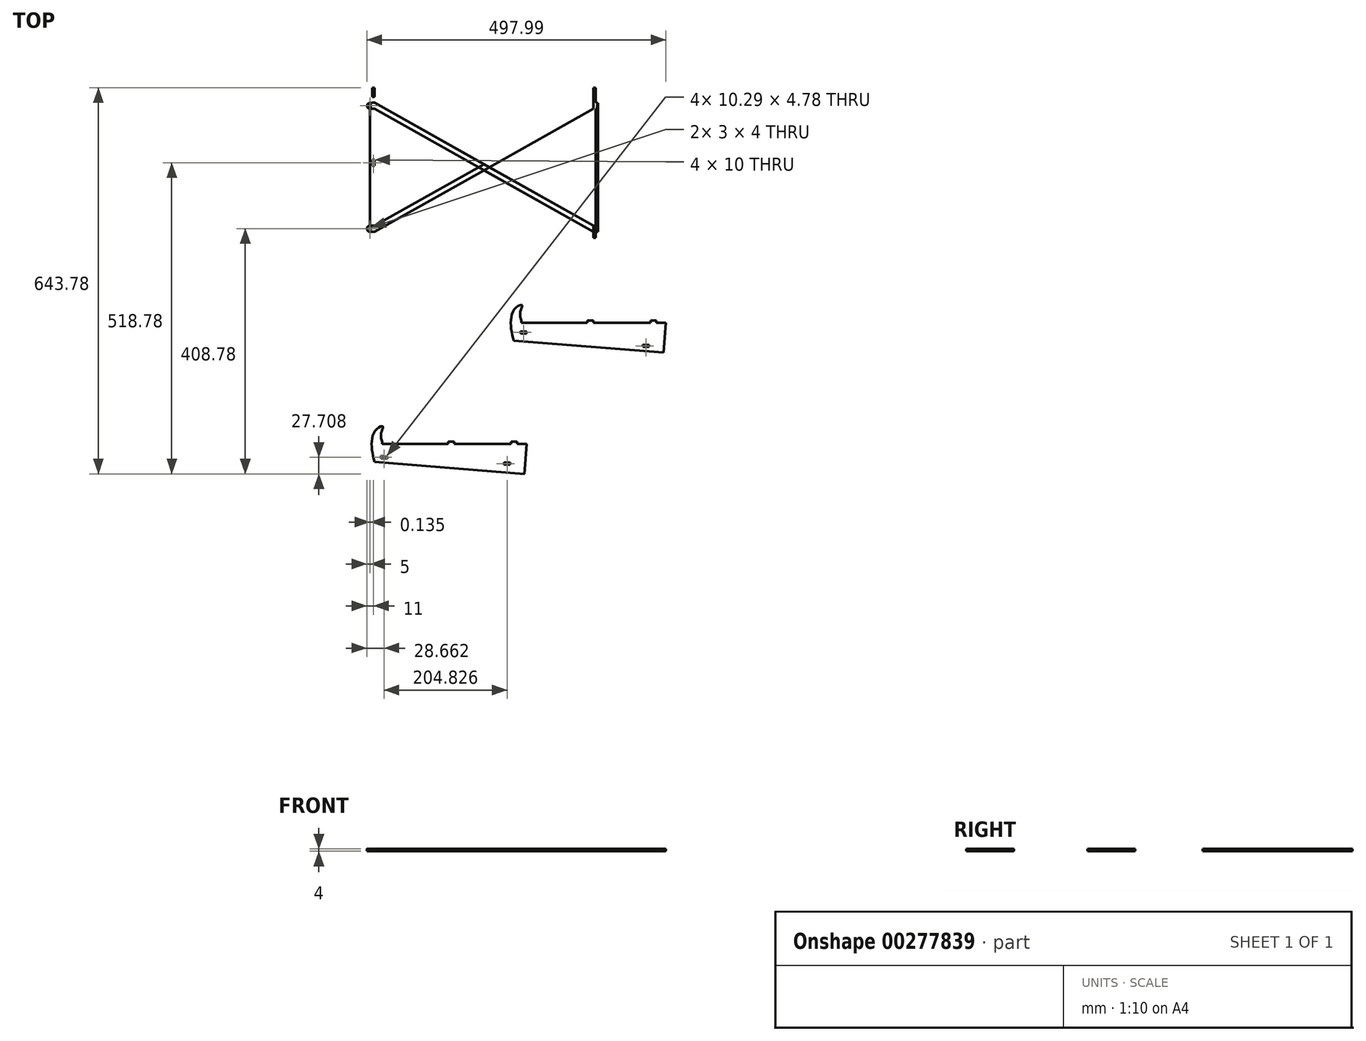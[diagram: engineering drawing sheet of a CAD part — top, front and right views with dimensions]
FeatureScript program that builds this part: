
annotation { "Feature Type Name" : "Feature", "Feature Type Description" : "" }
export const myFeature = defineFeature(function(context is Context, id is Id, definition is map)
    precondition{}
    {
        {
            var Q0;
            Q0=qCreatedBy(makeId("Top.planeOp"),FACE);
            var sketch = newSketch(context, id + "F0", { "sketchPlane" : qUnion([Q0])});
            skLineSegment(sketch, "E0.bottom", {"start": v(190, 125) * mm, "end": v(-190, 125) * mm});
            skLineSegment(sketch, "E0.top", {"start": v(190, -125) * mm, "end": v(-190, -125) * mm});
            skLineSegment(sketch, "E0.left", {"start": v(190, 125) * mm, "end": v(190, -125) * mm});
            skLineSegment(sketch, "E0.right", {"start": v(-190, 125) * mm, "end": v(-190, -125) * mm});
            skPoint(sketch, "E0.middle", {"position": v(0, 0) * mm});
            skLineSegment(sketch, "E1.right", {"start": v(-190, 125) * mm, "end": v(-190, -108) * mm});
            skLineSegment(sketch, "E2.bottom", {"start": v(-190, -125) * mm, "end": v(-186, -125) * mm});
            skLineSegment(sketch, "E2.top", {"start": v(-190, 125) * mm, "end": v(-186, 125) * mm});
            skLineSegment(sketch, "E2.left", {"start": v(-190, -125) * mm, "end": v(-190, -112) * mm});
            skLineSegment(sketch, "E2.right", {"start": v(-186, -125) * mm, "end": v(-186, -115) * mm});
            skLineSegment(sketch, "E3.bottom", {"start": v(190, -125) * mm, "end": v(186, -125) * mm});
            skLineSegment(sketch, "E3.top", {"start": v(190, 125) * mm, "end": v(186, 125) * mm});
            skLineSegment(sketch, "E3.left", {"start": v(190, -125) * mm, "end": v(190, 125) * mm});
            skLineSegment(sketch, "E3.right", {"start": v(186, -125) * mm, "end": v(186, 125) * mm});
            skLineSegment(sketch, "E4", {"start": v(49.8, -296.66) * mm, "end": v(299, -316.6) * mm});
            skLineSegment(sketch, "E5", {"start": v(299, -316.6) * mm, "end": v(303, -266.76) * mm});
            skLineSegment(sketch, "E6", {"start": v(303, -266.76) * mm, "end": v(287.2, -266.76) * mm});
            skLineSegment(sketch, "E7", {"start": v(52.2, -266.76) * mm, "end": v(49.8, -296.66) * mm, "construction": true});
            skLineSegment(sketch, "E8", {"start": v(0, 0) * mm, "end": v(0, 125) * mm, "construction": true});
            skLineSegment(sketch, "E9", {"start": v(0, 0) * mm, "end": v(0, -125) * mm, "construction": true});
            skLineSegment(sketch, "E10.bottom", {"start": v(-186, 125) * mm, "end": v(-182, 125) * mm});
            skLineSegment(sketch, "E10.top", {"start": v(-186, -125) * mm, "end": v(-182, -125) * mm});
            skLineSegment(sketch, "E10.left", {"start": v(-186, 125) * mm, "end": v(-186, 100) * mm});
            skLineSegment(sketch, "E10.right", {"start": v(-182, 125) * mm, "end": v(-182, 100) * mm});
            skLineSegment(sketch, "E11.MirrorCS", {"start": v(182, 125) * mm, "end": v(182, -125) * mm});
            skLineSegment(sketch, "E12", {"start": v(-186, -115) * mm, "end": v(-182, -115) * mm});
            skLineSegment(sketch, "E13", {"start": v(-186, 0) * mm, "end": v(186, 0) * mm, "construction": true});
            skLineSegment(sketch, "E14", {"start": v(-183.8, 0) * mm, "end": v(-183.8, 5) * mm, "construction": true});
            skLineSegment(sketch, "E15", {"start": v(-186, 5) * mm, "end": v(-182, 5) * mm});
            skLineSegment(sketch, "E16.MirrorCS", {"start": v(-186, -5) * mm, "end": v(-182, -5) * mm});
            skLineSegment(sketch, "E17", {"start": v(-186, 110) * mm, "end": v(-182, 110) * mm});
            skLineSegment(sketch, "E18", {"start": v(-186, 100) * mm, "end": v(-182, 100) * mm});
            skLineSegment(sketch, "E19", {"start": v(52.2, -266.76) * mm, "end": v(52.2, -242.76) * mm, "construction": true});
            skLineSegment(sketch, "E20", {"start": v(52.2, -242.76) * mm, "end": v(62.16, -243.56) * mm, "construction": true});
            skLineSegment(sketch, "E21", {"start": v(62.16, -243.56) * mm, "end": v(62.16, -266.76) * mm, "construction": true});
            skLineSegment(sketch, "E22.bottom", {"start": v(62.16, -266.76) * mm, "end": v(172.2, -266.76) * mm, "construction": true});
            skLineSegment(sketch, "E22.top", {"start": v(52.2, -262.76) * mm, "end": v(303, -262.76) * mm, "construction": true});
            skLineSegment(sketch, "E22.left", {"start": v(52.2, -266.76) * mm, "end": v(52.2, -262.76) * mm, "construction": true});
            skLineSegment(sketch, "E22.right", {"start": v(303, -266.76) * mm, "end": v(303, -262.76) * mm, "construction": true});
            skFitSpline(sketch, "E23", {"points": [v(49.8, -296.66) * mm, v(44.72, -265.8) * mm, v(52.2, -242.76) * mm, v(62.86, -237.24) * mm, v(62.38, -242.76) * mm, v(62.16, -262.76) * mm], "startDerivative": vector(-32.9, 108.57) * mm, "endDerivative": vector(52.9, -154.73) * mm});
            skLineSegment(sketch, "E24", {"start": v(62.16, -262.76) * mm, "end": v(62.16, -266.76) * mm});
            skLineSegment(sketch, "E25", {"start": v(302.2, -266.76) * mm, "end": v(302.2, -262.76) * mm, "construction": true});
            skLineSegment(sketch, "E26", {"start": v(287.2, -266.76) * mm, "end": v(287.2, -262.76) * mm});
            skLineSegment(sketch, "E27", {"start": v(287.2, -262.76) * mm, "end": v(277.2, -262.76) * mm});
            skLineSegment(sketch, "E28", {"start": v(277.2, -262.76) * mm, "end": v(277.2, -266.76) * mm});
            skLineSegment(sketch, "E29", {"start": v(182.2, -266.76) * mm, "end": v(182.2, -262.76) * mm});
            skLineSegment(sketch, "E30", {"start": v(172.2, -266.76) * mm, "end": v(172.2, -262.76) * mm});
            skLineSegment(sketch, "E31", {"start": v(172.2, -262.76) * mm, "end": v(182.2, -262.76) * mm});
            skLineSegment(sketch, "E32", {"start": v(-182, -105) * mm, "end": v(-186, -105) * mm});
            skLineSegment(sketch, "E33", {"start": v(-186, 90) * mm, "end": v(-182, 90) * mm});
            skLineSegment(sketch, "E34.MirrorCS", {"start": v(186, 125) * mm, "end": v(182, 125) * mm});
            skLineSegment(sketch, "E35.MirrorCS", {"start": v(186, -125) * mm, "end": v(182, -125) * mm});
            skLineSegment(sketch, "E36.MirrorCS", {"start": v(-190, -125) * mm, "end": v(190, -125) * mm});
            skLineSegment(sketch, "E37.MirrorCS", {"start": v(186, 110) * mm, "end": v(182, 110) * mm});
            skLineSegment(sketch, "E38.MirrorCS", {"start": v(183.8, 0) * mm, "end": v(183.8, 5) * mm, "construction": true});
            skLineSegment(sketch, "E39.MirrorCS", {"start": v(186, 100) * mm, "end": v(182, 100) * mm});
            skLineSegment(sketch, "E40.MirrorCS", {"start": v(182, -105) * mm, "end": v(186, -105) * mm});
            skLineSegment(sketch, "E41.MirrorCS", {"start": v(186, -5) * mm, "end": v(182, -5) * mm});
            skLineSegment(sketch, "E42.MirrorCS", {"start": v(186, 90) * mm, "end": v(182, 90) * mm});
            skLineSegment(sketch, "E43.MirrorCS", {"start": v(186, 5) * mm, "end": v(182, 5) * mm});
            skLineSegment(sketch, "E44.MirrorCS", {"start": v(186, -115) * mm, "end": v(182, -115) * mm});
            skLineSegment(sketch, "E45", {"start": v(-182, -115) * mm, "end": v(182, 90) * mm});
            skLineSegment(sketch, "E46", {"start": v(-182, -105) * mm, "end": v(182, 100) * mm});
            skLineSegment(sketch, "E47", {"start": v(-182, 90) * mm, "end": v(182, -115) * mm});
            skLineSegment(sketch, "E48", {"start": v(182, -105) * mm, "end": v(-182, 100) * mm});
            skLineSegment(sketch, "E49.trimOffspring", {"start": v(-186, -115) * mm, "end": v(-186, -125) * mm});
            skLineSegment(sketch, "E50.trimOffspring", {"start": v(-186, -105) * mm, "end": v(-186, 90) * mm});
            skLineSegment(sketch, "E51", {"start": v(-186, -105) * mm, "end": v(-190, -105) * mm});
            skLineSegment(sketch, "E52", {"start": v(-186, -115) * mm, "end": v(-190, -115) * mm});
            skArc(sketch, "E53", {"start": v(-190, -105) * mm, "mid": v(-195, -110) * mm, "end": v(-190, -115) * mm});
            skArc(sketch, "E54", {"start": v(-190, 99.76) * mm, "mid": v(-194.75, 94.88) * mm, "end": v(-190, 90) * mm});
            skLineSegment(sketch, "E55.trimOffspring", {"start": v(-186, 100) * mm, "end": v(-186, 125) * mm});
            skLineSegment(sketch, "E56.trimOffspring", {"start": v(-186, 90) * mm, "end": v(-186, -105) * mm});
            skLineSegment(sketch, "E57.trimOffspring", {"start": v(-182, 90) * mm, "end": v(-182, -125) * mm});
            skLineSegment(sketch, "E58.MirrorCS", {"start": v(186, -125) * mm, "end": v(186, -115) * mm});
            skLineSegment(sketch, "E59.MirrorCS", {"start": v(186, -115) * mm, "end": v(186, -125) * mm});
            skLineSegment(sketch, "E60.MirrorCS", {"start": v(186, -115) * mm, "end": v(190, -115) * mm});
            skLineSegment(sketch, "E61.MirrorCS", {"start": v(186, -105) * mm, "end": v(190, -105) * mm});
            skArc(sketch, "E62.MirrorCS", {"start": v(190, -105) * mm, "mid": v(195, -110) * mm, "end": v(190, -115) * mm});
            skLineSegment(sketch, "E63.MirrorCS", {"start": v(186, 100) * mm, "end": v(186, 125) * mm});
            skLineSegment(sketch, "E64.MirrorCS", {"start": v(182, 125) * mm, "end": v(182, 100) * mm});
            skLineSegment(sketch, "E65.MirrorCS", {"start": v(186, 125) * mm, "end": v(186, 100) * mm});
            skArc(sketch, "E66.MirrorCS", {"start": v(190, 99.76) * mm, "mid": v(194.75, 94.88) * mm, "end": v(190, 90) * mm});
            skLineSegment(sketch, "E67.MirrorCS", {"start": v(186, 90) * mm, "end": v(186, -105) * mm});
            skLineSegment(sketch, "E68.MirrorCS", {"start": v(186, -105) * mm, "end": v(186, 90) * mm});
            skLineSegment(sketch, "E69.MirrorCS", {"start": v(182, 90) * mm, "end": v(182, -125) * mm});
            skLineSegment(sketch, "E70", {"start": v(186, 100) * mm, "end": v(190, 99.76) * mm});
            skLineSegment(sketch, "E71", {"start": v(186, 90) * mm, "end": v(190, 90) * mm});
            skLineSegment(sketch, "E72", {"start": v(-186, 90) * mm, "end": v(-190, 90) * mm});
            skLineSegment(sketch, "E73", {"start": v(-186, 100) * mm, "end": v(-190, 99.76) * mm});
            skLineSegment(sketch, "E74.trimOffspring", {"start": v(182.2, -266.76) * mm, "end": v(277.2, -266.76) * mm, "construction": true});
            skLineSegment(sketch, "E75.trimOffspring", {"start": v(172.2, -266.76) * mm, "end": v(62.16, -266.76) * mm});
            skLineSegment(sketch, "E76.trimOffspring", {"start": v(287.2, -266.76) * mm, "end": v(303, -266.76) * mm, "construction": true});
            skLineSegment(sketch, "E77.trimOffspring", {"start": v(277.2, -266.76) * mm, "end": v(182.2, -266.76) * mm});
            skLineSegment(sketch, "E78", {"start": v(50.84, -283.7) * mm, "end": v(300.04, -303.64) * mm, "construction": true});
            skLineSegment(sketch, "E79", {"start": v(51.16, -279.72) * mm, "end": v(300.36, -299.66) * mm, "construction": true});
            skLineSegment(sketch, "E80", {"start": v(275.12, -301.65) * mm, "end": v(275.44, -297.66) * mm});
            skLineSegment(sketch, "E81", {"start": v(275.44, -297.66) * mm, "end": v(265.47, -296.86) * mm});
            skLineSegment(sketch, "E82", {"start": v(265.47, -296.86) * mm, "end": v(265.15, -300.85) * mm});
            skLineSegment(sketch, "E83", {"start": v(265.15, -300.85) * mm, "end": v(275.12, -301.65) * mm});
            skLineSegment(sketch, "E84", {"start": v(60.8, -284.5) * mm, "end": v(61.13, -280.52) * mm});
            skLineSegment(sketch, "E85", {"start": v(71.1, -281.31) * mm, "end": v(70.77, -285.3) * mm});
            skLineSegment(sketch, "E86", {"start": v(61.13, -280.52) * mm, "end": v(71.1, -281.31) * mm});
            skLineSegment(sketch, "E87", {"start": v(70.77, -285.3) * mm, "end": v(60.8, -284.5) * mm});
            skLineSegment(sketch, "E88", {"start": v(265.47, -296.86) * mm, "end": v(264.12, -313.81) * mm, "construction": true});
            skLineSegment(sketch, "E89", {"start": v(275.44, -297.66) * mm, "end": v(274.09, -314.6) * mm, "construction": true});
            skLineSegment(sketch, "E90", {"start": v(264.68, -306.83) * mm, "end": v(274.64, -307.63) * mm});
            skLineSegment(sketch, "E91", {"start": v(265, -302.85) * mm, "end": v(274.96, -303.64) * mm});
            skLineSegment(sketch, "E92", {"start": v(265, -302.85) * mm, "end": v(264.68, -306.83) * mm});
            skLineSegment(sketch, "E93", {"start": v(274.96, -303.64) * mm, "end": v(274.64, -307.63) * mm});
            skLineSegment(sketch, "E94", {"start": v(61.13, -280.52) * mm, "end": v(59.77, -297.46) * mm, "construction": true});
            skLineSegment(sketch, "E95", {"start": v(60.65, -286.5) * mm, "end": v(70.62, -287.3) * mm});
            skLineSegment(sketch, "E96", {"start": v(60.33, -290.48) * mm, "end": v(70.3, -291.28) * mm});
            skLineSegment(sketch, "E97", {"start": v(70.3, -291.28) * mm, "end": v(70.62, -287.3) * mm});
            skLineSegment(sketch, "E98", {"start": v(60.65, -286.5) * mm, "end": v(60.33, -290.48) * mm});
            skLineSegment(sketch, "E99", {"start": v(-182, -498.85) * mm, "end": v(67.2, -518.78) * mm});
            skLineSegment(sketch, "E100", {"start": v(67.2, -518.78) * mm, "end": v(71.18, -468.94) * mm});
            skLineSegment(sketch, "E101", {"start": v(71.18, -468.94) * mm, "end": v(55.38, -468.94) * mm});
            skLineSegment(sketch, "E102", {"start": v(-179.62, -468.94) * mm, "end": v(-182, -498.85) * mm, "construction": true});
            skLineSegment(sketch, "E103", {"start": v(-179.62, -468.94) * mm, "end": v(-179.62, -444.94) * mm, "construction": true});
            skLineSegment(sketch, "E104", {"start": v(-179.62, -444.94) * mm, "end": v(-169.65, -445.74) * mm, "construction": true});
            skLineSegment(sketch, "E105", {"start": v(-169.65, -445.74) * mm, "end": v(-169.65, -468.94) * mm, "construction": true});
            skLineSegment(sketch, "E106.bottom", {"start": v(-169.65, -468.94) * mm, "end": v(-59.62, -468.94) * mm, "construction": true});
            skLineSegment(sketch, "E106.top", {"start": v(-179.62, -464.94) * mm, "end": v(71.18, -464.94) * mm, "construction": true});
            skLineSegment(sketch, "E106.left", {"start": v(-179.62, -468.94) * mm, "end": v(-179.62, -464.94) * mm, "construction": true});
            skLineSegment(sketch, "E106.right", {"start": v(71.18, -468.94) * mm, "end": v(71.18, -464.94) * mm, "construction": true});
            skFitSpline(sketch, "E107", {"points": [v(-182, -498.85) * mm, v(-187.09, -467.99) * mm, v(-179.62, -444.94) * mm, v(-168.95, -439.42) * mm, v(-169.43, -444.94) * mm, v(-169.65, -464.94) * mm], "startDerivative": vector(-32.9, 108.57) * mm, "endDerivative": vector(52.9, -154.73) * mm});
            skLineSegment(sketch, "E108", {"start": v(-169.65, -464.94) * mm, "end": v(-169.65, -468.94) * mm});
            skLineSegment(sketch, "E109", {"start": v(70.38, -468.94) * mm, "end": v(70.38, -464.94) * mm, "construction": true});
            skLineSegment(sketch, "E110", {"start": v(55.38, -468.94) * mm, "end": v(55.38, -464.94) * mm});
            skLineSegment(sketch, "E111", {"start": v(55.38, -464.94) * mm, "end": v(45.38, -464.94) * mm});
            skLineSegment(sketch, "E112", {"start": v(45.38, -464.94) * mm, "end": v(45.38, -468.94) * mm});
            skLineSegment(sketch, "E113", {"start": v(-49.62, -468.94) * mm, "end": v(-49.62, -464.94) * mm});
            skLineSegment(sketch, "E114", {"start": v(-59.62, -468.94) * mm, "end": v(-59.62, -464.94) * mm});
            skLineSegment(sketch, "E115", {"start": v(-59.62, -464.94) * mm, "end": v(-49.62, -464.94) * mm});
            skLineSegment(sketch, "E116.trimOffspring", {"start": v(-49.62, -468.94) * mm, "end": v(45.38, -468.94) * mm, "construction": true});
            skLineSegment(sketch, "E117.trimOffspring", {"start": v(-59.62, -468.94) * mm, "end": v(-169.65, -468.94) * mm});
            skLineSegment(sketch, "E118.trimOffspring", {"start": v(55.38, -468.94) * mm, "end": v(71.18, -468.94) * mm, "construction": true});
            skLineSegment(sketch, "E119.trimOffspring", {"start": v(45.38, -468.94) * mm, "end": v(-49.62, -468.94) * mm});
            skLineSegment(sketch, "E120", {"start": v(-180.97, -485.89) * mm, "end": v(68.23, -505.82) * mm, "construction": true});
            skLineSegment(sketch, "E121", {"start": v(-180.65, -481.9) * mm, "end": v(68.55, -501.84) * mm, "construction": true});
            skLineSegment(sketch, "E122", {"start": v(43.31, -503.83) * mm, "end": v(43.63, -499.84) * mm});
            skLineSegment(sketch, "E123", {"start": v(43.63, -499.84) * mm, "end": v(33.66, -499.05) * mm});
            skLineSegment(sketch, "E124", {"start": v(33.66, -499.05) * mm, "end": v(33.34, -503.03) * mm});
            skLineSegment(sketch, "E125", {"start": v(33.34, -503.03) * mm, "end": v(43.31, -503.83) * mm});
            skLineSegment(sketch, "E126", {"start": v(-171, -486.69) * mm, "end": v(-170.68, -482.7) * mm});
            skLineSegment(sketch, "E127", {"start": v(-160.72, -483.5) * mm, "end": v(-161.03, -487.48) * mm});
            skLineSegment(sketch, "E128", {"start": v(-170.68, -482.7) * mm, "end": v(-160.72, -483.5) * mm});
            skLineSegment(sketch, "E129", {"start": v(-161.03, -487.48) * mm, "end": v(-171, -486.69) * mm});
            skLineSegment(sketch, "E130", {"start": v(33.66, -499.05) * mm, "end": v(32.3, -516) * mm, "construction": true});
            skLineSegment(sketch, "E131", {"start": v(43.63, -499.84) * mm, "end": v(42.28, -516.79) * mm, "construction": true});
            skLineSegment(sketch, "E132", {"start": v(32.87, -509.01) * mm, "end": v(42.83, -509.81) * mm});
            skLineSegment(sketch, "E133", {"start": v(33.19, -505.03) * mm, "end": v(43.15, -505.82) * mm});
            skLineSegment(sketch, "E134", {"start": v(33.19, -505.03) * mm, "end": v(32.87, -509.01) * mm});
            skLineSegment(sketch, "E135", {"start": v(43.15, -505.82) * mm, "end": v(42.83, -509.81) * mm});
            skLineSegment(sketch, "E136", {"start": v(-170.68, -482.7) * mm, "end": v(-172.04, -499.64) * mm, "construction": true});
            skLineSegment(sketch, "E137", {"start": v(-171.16, -488.68) * mm, "end": v(-161.2, -489.48) * mm});
            skLineSegment(sketch, "E138", {"start": v(-171.48, -492.67) * mm, "end": v(-161.51, -493.46) * mm});
            skLineSegment(sketch, "E139", {"start": v(-161.51, -493.46) * mm, "end": v(-161.2, -489.48) * mm});
            skLineSegment(sketch, "E140", {"start": v(-171.16, -488.68) * mm, "end": v(-171.48, -492.67) * mm});
            skLineSegment(sketch, "E141.bottom", {"start": v(-188.5, -108) * mm, "end": v(-191.5, -108) * mm});
            skLineSegment(sketch, "E141.top", {"start": v(-188.5, -112) * mm, "end": v(-191.5, -112) * mm});
            skLineSegment(sketch, "E141.left", {"start": v(-188.5, -108) * mm, "end": v(-188.5, -112) * mm});
            skLineSegment(sketch, "E141.right", {"start": v(-191.5, -108) * mm, "end": v(-191.5, -112) * mm});
            skLineSegment(sketch, "E142.MirrorCS", {"start": v(-190, -125) * mm, "end": v(-190, 125) * mm});
            skLineSegment(sketch, "E143.trimOffspring", {"start": v(-190, -108) * mm, "end": v(-190, 125) * mm});
            skLineSegment(sketch, "E144.trimOffspring", {"start": v(-190, -110) * mm, "end": v(-190, -125) * mm});
            skLineSegment(sketch, "E145.bottom", {"start": v(-191.37, 96.88) * mm, "end": v(-188.37, 96.88) * mm});
            skLineSegment(sketch, "E145.top", {"start": v(-191.37, 92.88) * mm, "end": v(-188.37, 92.88) * mm});
            skLineSegment(sketch, "E145.left", {"start": v(-191.37, 96.88) * mm, "end": v(-191.37, 92.88) * mm});
            skLineSegment(sketch, "E145.right", {"start": v(-188.37, 96.88) * mm, "end": v(-188.37, 92.88) * mm});
            skLineSegment(sketch, "E146.MirrorCS", {"start": v(191.37, 92.88) * mm, "end": v(188.37, 92.88) * mm});
            skLineSegment(sketch, "E147.MirrorCS", {"start": v(191.37, 96.88) * mm, "end": v(188.37, 96.88) * mm});
            skLineSegment(sketch, "E148.MirrorCS", {"start": v(191.37, 96.88) * mm, "end": v(191.37, 92.88) * mm});
            skLineSegment(sketch, "E149.MirrorCS", {"start": v(188.37, 96.88) * mm, "end": v(188.37, 92.88) * mm});
            skLineSegment(sketch, "E150.MirrorCS", {"start": v(188.5, -112) * mm, "end": v(191.5, -112) * mm});
            skLineSegment(sketch, "E151.MirrorCS", {"start": v(188.5, -108) * mm, "end": v(191.5, -108) * mm});
            skLineSegment(sketch, "E152.MirrorCS", {"start": v(191.5, -108) * mm, "end": v(191.5, -112) * mm});
            skLineSegment(sketch, "E153.MirrorCS", {"start": v(188.5, -108) * mm, "end": v(188.5, -112) * mm});
            skSolve(sketch);
        }
        {
            var Q0;
            {var subQ0=sQuery(id+"F0.wireOp",EDGE,"E42.MirrorCS");Q0=makeQuery(id+"F0.imprint","IMPRINT",FACE,{"disambiguationData":[TD([[makeQuery(id+"F0.imprint","IMPRINT",EDGE,{"derivedFrom":subQ0}),1.0]])]});}
            var Q1;
            {var subQ0=sQuery(id+"F0.wireOp",EDGE,"E47");var subQ1=sQuery(id+"F0.wireOp",EDGE,"E45");var subQ2=makeQuery(id+"F0.imprint","INTERSECT",VERTEX,{"derivedFrom":[subQ1,subQ0]});Q1=makeQuery(id+"F0.imprint","IMPRINT",FACE,{"disambiguationData":[TD([[makeQuery(id+"F0.imprint","IMPRINT",EDGE,{"disambiguationData":[TD([[subQ2,-1.0]])],"derivedFrom":subQ1}),-1.0]])]});}
            var Q2;
            {var subQ8=sQuery(id+"F0.wireOp",EDGE,"E0.bottom");Q2=makeQuery(id+"F0.imprint","IMPRINT",FACE,{"disambiguationData":[TD([[makeQuery(id+"F0.imprint","IMPRINT",EDGE,{"derivedFrom":subQ8}),1.0]])]});}
            var Q3;
            {var subQ14=sQuery(id+"F0.wireOp",EDGE,"E2.top");Q3=makeQuery(id+"F0.imprint","IMPRINT",FACE,{"disambiguationData":[TD([[makeQuery(id+"F0.imprint","IMPRINT",EDGE,{"derivedFrom":subQ14}),-1.0]])]});}
            var Q4;
            {var subQ0=sQuery(id+"F0.wireOp",EDGE,"E11.MirrorCS");Q4=makeQuery(id+"F0.imprint","IMPRINT",FACE,{"disambiguationData":[TD([[makeQuery(id+"F0.imprint","IMPRINT",EDGE,{"derivedFrom":subQ0}),-1.0]])]});}
            var Q5;
            {var subQ0=sQuery(id+"F0.wireOp",EDGE,"E40.MirrorCS");Q5=makeQuery(id+"F0.imprint","IMPRINT",FACE,{"disambiguationData":[TD([[makeQuery(id+"F0.imprint","IMPRINT",EDGE,{"derivedFrom":subQ0}),1.0]])]});}
            var Q6;
            {var subQ0=sQuery(id+"F0.wireOp",EDGE,"E15");Q6=makeQuery(id+"F0.imprint","IMPRINT",FACE,{"disambiguationData":[TD([[makeQuery(id+"F0.imprint","IMPRINT",EDGE,{"derivedFrom":subQ0}),1.0]])]});}
            var Q7;
            {var subQ0=sQuery(id+"F0.wireOp",EDGE,"E34.MirrorCS");Q7=makeQuery(id+"F0.imprint","IMPRINT",FACE,{"disambiguationData":[TD([[makeQuery(id+"F0.imprint","IMPRINT",EDGE,{"derivedFrom":subQ0}),1.0]])]});}
            var Q8;
            {var subQ0=sQuery(id+"F0.wireOp",EDGE,"E69.MirrorCS");var subQ3=makeQuery(id+"F0.imprint","INTERSECT",VERTEX,{"derivedFrom":[sQuery(id+"F0.wireOp",EDGE,"E43.MirrorCS"),subQ0]});Q8=makeQuery(id+"F0.imprint","IMPRINT",FACE,{"disambiguationData":[TD([[makeQuery(id+"F0.imprint","IMPRINT",EDGE,{"disambiguationData":[TD([[subQ3,-1.0]])],"derivedFrom":subQ0}),-1.0]])]});}
            var Q9;
            {var subQ0=sQuery(id+"F0.wireOp",EDGE,"E16.MirrorCS");Q9=makeQuery(id+"F0.imprint","IMPRINT",FACE,{"disambiguationData":[TD([[makeQuery(id+"F0.imprint","IMPRINT",EDGE,{"derivedFrom":subQ0}),-1.0]])]});}
            var Q10;
            {var subQ0=sQuery(id+"F0.wireOp",EDGE,"E10.bottom");Q10=makeQuery(id+"F0.imprint","IMPRINT",FACE,{"disambiguationData":[TD([[makeQuery(id+"F0.imprint","IMPRINT",EDGE,{"derivedFrom":subQ0}),-1.0]])]});}
            var Q11;
            {var subQ0=sQuery(id+"F0.wireOp",EDGE,"E57.trimOffspring");var subQ1=makeQuery(id+"F0.imprint","INTERSECT",VERTEX,{"derivedFrom":[sQuery(id+"F0.wireOp",EDGE,"E15"),subQ0]});Q11=makeQuery(id+"F0.imprint","IMPRINT",FACE,{"disambiguationData":[TD([[makeQuery(id+"F0.imprint","IMPRINT",EDGE,{"disambiguationData":[TD([[subQ1,-1.0]])],"derivedFrom":subQ0}),1.0]])]});}
            var Q12;
            {var subQ0=sQuery(id+"F0.wireOp",EDGE,"E57.trimOffspring");var subQ3=sQuery(id+"F0.wireOp",EDGE,"E36.MirrorCS");var subQ4=makeQuery(id+"F0.imprint","INTERSECT",VERTEX,{"derivedFrom":[subQ3,subQ0]});Q12=makeQuery(id+"F0.imprint","IMPRINT",FACE,{"disambiguationData":[TD([[makeQuery(id+"F0.imprint","IMPRINT",EDGE,{"disambiguationData":[TD([[subQ4,-1.0]])],"derivedFrom":subQ3}),1.0]])]});}
            var Q13;
            {var subQ1=sQuery(id+"F0.wireOp",EDGE,"E45");var subQ3=sQuery(id+"F0.wireOp",EDGE,"E47");var subQ4=makeQuery(id+"F0.imprint","INTERSECT",VERTEX,{"derivedFrom":[subQ1,subQ3]});Q13=makeQuery(id+"F0.imprint","IMPRINT",FACE,{"disambiguationData":[TD([[makeQuery(id+"F0.imprint","IMPRINT",EDGE,{"disambiguationData":[TD([[subQ4,1.0]])],"derivedFrom":subQ3}),-1.0]])]});}
            var Q14;
            {var subQ0=sQuery(id+"F0.wireOp",EDGE,"E47");var subQ1=sQuery(id+"F0.wireOp",EDGE,"E45");var subQ2=makeQuery(id+"F0.imprint","INTERSECT",VERTEX,{"derivedFrom":[subQ1,subQ0]});Q14=makeQuery(id+"F0.imprint","IMPRINT",FACE,{"disambiguationData":[TD([[makeQuery(id+"F0.imprint","IMPRINT",EDGE,{"disambiguationData":[TD([[subQ2,-1.0]])],"derivedFrom":subQ1}),1.0]])]});}
            var Q15;
            {var subQ1=sQuery(id+"F0.wireOp",EDGE,"E61.MirrorCS");Q15=makeQuery(id+"F0.imprint","IMPRINT",FACE,{"disambiguationData":[TD([[makeQuery(id+"F0.imprint","IMPRINT",EDGE,{"derivedFrom":subQ1}),1.0]])]});}
            var Q16;
            {var subQ1=sQuery(id+"F0.wireOp",EDGE,"E3.top");Q16=makeQuery(id+"F0.imprint","IMPRINT",FACE,{"disambiguationData":[TD([[makeQuery(id+"F0.imprint","IMPRINT",EDGE,{"derivedFrom":subQ1}),1.0]])]});}
            var Q17;
            {var subQ1=sQuery(id+"F0.wireOp",EDGE,"E12");Q17=makeQuery(id+"F0.imprint","IMPRINT",FACE,{"disambiguationData":[TD([[makeQuery(id+"F0.imprint","IMPRINT",EDGE,{"derivedFrom":subQ1}),1.0]])]});}
            var Q18;
            Q18=makeQuery(id+"F0.imprint","IMPRINT",FACE,{"disambiguationData":[TD([[makeQuery(id+"F0.imprint","IMPRINT",EDGE,{"derivedFrom":sQuery(id+"F0.wireOp",EDGE,"E11.MirrorCS")}),1.0]])]});
            var Q19;
            {var subQ4=sQuery(id+"F0.wireOp",EDGE,"E49.trimOffspring");Q19=makeQuery(id+"F0.imprint","IMPRINT",FACE,{"disambiguationData":[TD([[makeQuery(id+"F0.imprint","IMPRINT",EDGE,{"derivedFrom":subQ4}),-1.0]])]});}
            var Q20;
            {var subQ0=sQuery(id+"F0.wireOp",EDGE,"E70");Q20=makeQuery(id+"F0.imprint","IMPRINT",FACE,{"disambiguationData":[TD([[makeQuery(id+"F0.imprint","IMPRINT",EDGE,{"derivedFrom":subQ0}),-1.0]])]});}
            var Q21;
            {var subQ0=sQuery(id+"F0.wireOp",EDGE,"E60.MirrorCS");Q21=makeQuery(id+"F0.imprint","IMPRINT",FACE,{"disambiguationData":[TD([[makeQuery(id+"F0.imprint","IMPRINT",EDGE,{"derivedFrom":subQ0}),1.0]])]});}
            var Q22;
            {var subQ0=sQuery(id+"F0.wireOp",EDGE,"E44.MirrorCS");Q22=makeQuery(id+"F0.imprint","IMPRINT",FACE,{"disambiguationData":[TD([[makeQuery(id+"F0.imprint","IMPRINT",EDGE,{"derivedFrom":subQ0}),-1.0]])]});}
            var Q23;
            {var subQ0=sQuery(id+"F0.wireOp",EDGE,"E3.bottom");Q23=makeQuery(id+"F0.imprint","IMPRINT",FACE,{"disambiguationData":[TD([[makeQuery(id+"F0.imprint","IMPRINT",EDGE,{"derivedFrom":subQ0}),-1.0]])]});}
            var Q24;
            {var subQ6=sQuery(id+"F0.wireOp",EDGE,"E18");Q24=makeQuery(id+"F0.imprint","IMPRINT",FACE,{"disambiguationData":[TD([[makeQuery(id+"F0.imprint","IMPRINT",EDGE,{"derivedFrom":subQ6}),-1.0]])]});}
            var Q25;
            {var subQ3=sQuery(id+"F0.wireOp",EDGE,"E51");Q25=makeQuery(id+"F0.imprint","IMPRINT",FACE,{"disambiguationData":[TD([[makeQuery(id+"F0.imprint","IMPRINT",EDGE,{"derivedFrom":subQ3}),-1.0]])]});}
            var Q26;
            {var subQ1=sQuery(id+"F0.wireOp",EDGE,"E141.left");Q26=makeQuery(id+"F0.imprint","IMPRINT",FACE,{"disambiguationData":[TD([[makeQuery(id+"F0.imprint","IMPRINT",EDGE,{"derivedFrom":subQ1}),-1.0]])]});}
            var Q27;
            {var subQ5=sQuery(id+"F0.wireOp",EDGE,"E145.right");Q27=makeQuery(id+"F0.imprint","IMPRINT",FACE,{"disambiguationData":[TD([[makeQuery(id+"F0.imprint","IMPRINT",EDGE,{"derivedFrom":subQ5}),-1.0]])]});}
            var Q28;
            {var subQ5=sQuery(id+"F0.wireOp",EDGE,"E149.MirrorCS");Q28=makeQuery(id+"F0.imprint","IMPRINT",FACE,{"disambiguationData":[TD([[makeQuery(id+"F0.imprint","IMPRINT",EDGE,{"derivedFrom":subQ5}),1.0]])]});}
            var Q29;
            {var subQ5=sQuery(id+"F0.wireOp",EDGE,"E153.MirrorCS");Q29=makeQuery(id+"F0.imprint","IMPRINT",FACE,{"disambiguationData":[TD([[makeQuery(id+"F0.imprint","IMPRINT",EDGE,{"derivedFrom":subQ5}),1.0]])]});}
            extrude(context, id + "F1", {"entities" : qUnion([Q0, Q1, Q2, Q3, Q4, Q5, Q6, Q7, Q8, Q9, Q10, Q11, Q12, Q13, Q14, Q15, Q16, Q17, Q18, Q19, Q20, Q21, Q22, Q23, Q24, Q25, Q26, Q27, Q28, Q29]), "depth" : 4 * mm});
        }
        {
            var Q0;
            {var subQ5=sQuery(id+"F0.wireOp",EDGE,"E18");Q0=makeQuery(id+"F0.imprint","IMPRINT",FACE,{"disambiguationData":[TD([[makeQuery(id+"F0.imprint","IMPRINT",EDGE,{"derivedFrom":subQ5}),-1.0]])]});}
            var Q1;
            {var subQ0=sQuery(id+"F0.wireOp",EDGE,"E54");Q1=makeQuery(id+"F0.imprint","IMPRINT",FACE,{"disambiguationData":[TD([[makeQuery(id+"F0.imprint","IMPRINT",EDGE,{"derivedFrom":subQ0}),1.0]])]});}
            var Q2;
            {var subQ0=sQuery(id+"F0.wireOp",EDGE,"E47");var subQ1=sQuery(id+"F0.wireOp",EDGE,"E45");var subQ2=makeQuery(id+"F0.imprint","INTERSECT",VERTEX,{"derivedFrom":[subQ1,subQ0]});Q2=makeQuery(id+"F0.imprint","IMPRINT",FACE,{"disambiguationData":[TD([[makeQuery(id+"F0.imprint","IMPRINT",EDGE,{"disambiguationData":[TD([[subQ2,-1.0]])],"derivedFrom":subQ1}),1.0]])]});}
            var Q3;
            {var subQ0=sQuery(id+"F0.wireOp",EDGE,"E47");var subQ1=sQuery(id+"F0.wireOp",EDGE,"E45");var subQ2=makeQuery(id+"F0.imprint","INTERSECT",VERTEX,{"derivedFrom":[subQ1,subQ0]});Q3=makeQuery(id+"F0.imprint","IMPRINT",FACE,{"disambiguationData":[TD([[makeQuery(id+"F0.imprint","IMPRINT",EDGE,{"disambiguationData":[TD([[subQ2,-1.0]])],"derivedFrom":subQ1}),-1.0]])]});}
            var Q4;
            {var subQ0=sQuery(id+"F0.wireOp",EDGE,"E44.MirrorCS");Q4=makeQuery(id+"F0.imprint","IMPRINT",FACE,{"disambiguationData":[TD([[makeQuery(id+"F0.imprint","IMPRINT",EDGE,{"derivedFrom":subQ0}),-1.0]])]});}
            var Q5;
            {var subQ0=sQuery(id+"F0.wireOp",EDGE,"E62.MirrorCS");Q5=makeQuery(id+"F0.imprint","IMPRINT",FACE,{"disambiguationData":[TD([[makeQuery(id+"F0.imprint","IMPRINT",EDGE,{"derivedFrom":subQ0}),-1.0]])]});}
            var Q6;
            {var subQ0=sQuery(id+"F0.wireOp",EDGE,"E60.MirrorCS");Q6=makeQuery(id+"F0.imprint","IMPRINT",FACE,{"disambiguationData":[TD([[makeQuery(id+"F0.imprint","IMPRINT",EDGE,{"derivedFrom":subQ0}),1.0]])]});}
            extrude(context, id + "F2", {"entities" : qUnion([Q0, Q1, Q2, Q3, Q4, Q5, Q6]), "depth" : 4 * mm});
        }
        {
            var Q0;
            {var subQ1=sQuery(id+"F0.wireOp",EDGE,"E45");var subQ3=sQuery(id+"F0.wireOp",EDGE,"E47");var subQ4=makeQuery(id+"F0.imprint","INTERSECT",VERTEX,{"derivedFrom":[subQ1,subQ3]});Q0=makeQuery(id+"F0.imprint","IMPRINT",FACE,{"disambiguationData":[TD([[makeQuery(id+"F0.imprint","IMPRINT",EDGE,{"disambiguationData":[TD([[subQ4,1.0]])],"derivedFrom":subQ3}),-1.0]])]});}
            var Q1;
            {var subQ1=sQuery(id+"F0.wireOp",EDGE,"E12");Q1=makeQuery(id+"F0.imprint","IMPRINT",FACE,{"disambiguationData":[TD([[makeQuery(id+"F0.imprint","IMPRINT",EDGE,{"derivedFrom":subQ1}),1.0]])]});}
            var Q2;
            {var subQ0=sQuery(id+"F0.wireOp",EDGE,"E53");Q2=makeQuery(id+"F0.imprint","IMPRINT",FACE,{"disambiguationData":[TD([[makeQuery(id+"F0.imprint","IMPRINT",EDGE,{"derivedFrom":subQ0}),1.0]])]});}
            var Q3;
            {var subQ0=sQuery(id+"F0.wireOp",EDGE,"E47");var subQ1=sQuery(id+"F0.wireOp",EDGE,"E45");var subQ2=makeQuery(id+"F0.imprint","INTERSECT",VERTEX,{"derivedFrom":[subQ1,subQ0]});Q3=makeQuery(id+"F0.imprint","IMPRINT",FACE,{"disambiguationData":[TD([[makeQuery(id+"F0.imprint","IMPRINT",EDGE,{"disambiguationData":[TD([[subQ2,-1.0]])],"derivedFrom":subQ1}),1.0]])]});}
            var Q4;
            {var subQ0=sQuery(id+"F0.wireOp",EDGE,"E11.MirrorCS");Q4=makeQuery(id+"F0.imprint","IMPRINT",FACE,{"disambiguationData":[TD([[makeQuery(id+"F0.imprint","IMPRINT",EDGE,{"derivedFrom":subQ0}),-1.0]])]});}
            var Q5;
            Q5=makeQuery(id+"F0.imprint","IMPRINT",FACE,{"disambiguationData":[TD([[makeQuery(id+"F0.imprint","IMPRINT",EDGE,{"derivedFrom":sQuery(id+"F0.wireOp",EDGE,"E11.MirrorCS")}),1.0]])]});
            var Q6;
            {var subQ0=sQuery(id+"F0.wireOp",EDGE,"E70");Q6=makeQuery(id+"F0.imprint","IMPRINT",FACE,{"disambiguationData":[TD([[makeQuery(id+"F0.imprint","IMPRINT",EDGE,{"derivedFrom":subQ0}),-1.0]])]});}
            var Q7;
            {var subQ0=sQuery(id+"F0.wireOp",EDGE,"E66.MirrorCS");Q7=makeQuery(id+"F0.imprint","IMPRINT",FACE,{"disambiguationData":[TD([[makeQuery(id+"F0.imprint","IMPRINT",EDGE,{"derivedFrom":subQ0}),-1.0]])]});}
            extrude(context, id + "F3", {"entities" : qUnion([Q0, Q1, Q2, Q3, Q4, Q5, Q6, Q7]), "depth" : 4 * mm});
        }
        {
            var Q0;
            Q0=makeQuery(id+"F0.imprint","IMPRINT",FACE,{"disambiguationData":[TD([[makeQuery(id+"F0.imprint","IMPRINT",EDGE,{"derivedFrom":sQuery(id+"F0.wireOp",EDGE,"E80")}),1.0]])]});
            var Q1;
            Q1=makeQuery(id+"F0.imprint","IMPRINT",FACE,{"disambiguationData":[TD([[makeQuery(id+"F0.imprint","IMPRINT",EDGE,{"derivedFrom":sQuery(id+"F0.wireOp",EDGE,"E4")}),1.0]])]});
            var Q2;
            Q2=makeQuery(id+"F0.imprint","IMPRINT",FACE,{"disambiguationData":[TD([[makeQuery(id+"F0.imprint","IMPRINT",EDGE,{"derivedFrom":sQuery(id+"F0.wireOp",EDGE,"E95")}),-1.0]])]});
            extrude(context, id + "F4", {"entities" : qUnion([Q0, Q1, Q2]), "depth" : 4 * mm});
        }
        {
            var Q0;
            Q0=makeQuery(id+"F0.imprint","IMPRINT",FACE,{"disambiguationData":[TD([[makeQuery(id+"F0.imprint","IMPRINT",EDGE,{"derivedFrom":sQuery(id+"F0.wireOp",EDGE,"E99")}),1.0]])]});
            var Q1;
            Q1=makeQuery(id+"F0.imprint","IMPRINT",FACE,{"disambiguationData":[TD([[makeQuery(id+"F0.imprint","IMPRINT",EDGE,{"derivedFrom":sQuery(id+"F0.wireOp",EDGE,"E126")}),-1.0]])]});
            var Q2;
            Q2=makeQuery(id+"F0.imprint","IMPRINT",FACE,{"disambiguationData":[TD([[makeQuery(id+"F0.imprint","IMPRINT",EDGE,{"derivedFrom":sQuery(id+"F0.wireOp",EDGE,"E132")}),1.0]])]});
            extrude(context, id + "F5", {"entities" : qUnion([Q0, Q1, Q2]), "depth" : 4 * mm});
        }
    });
